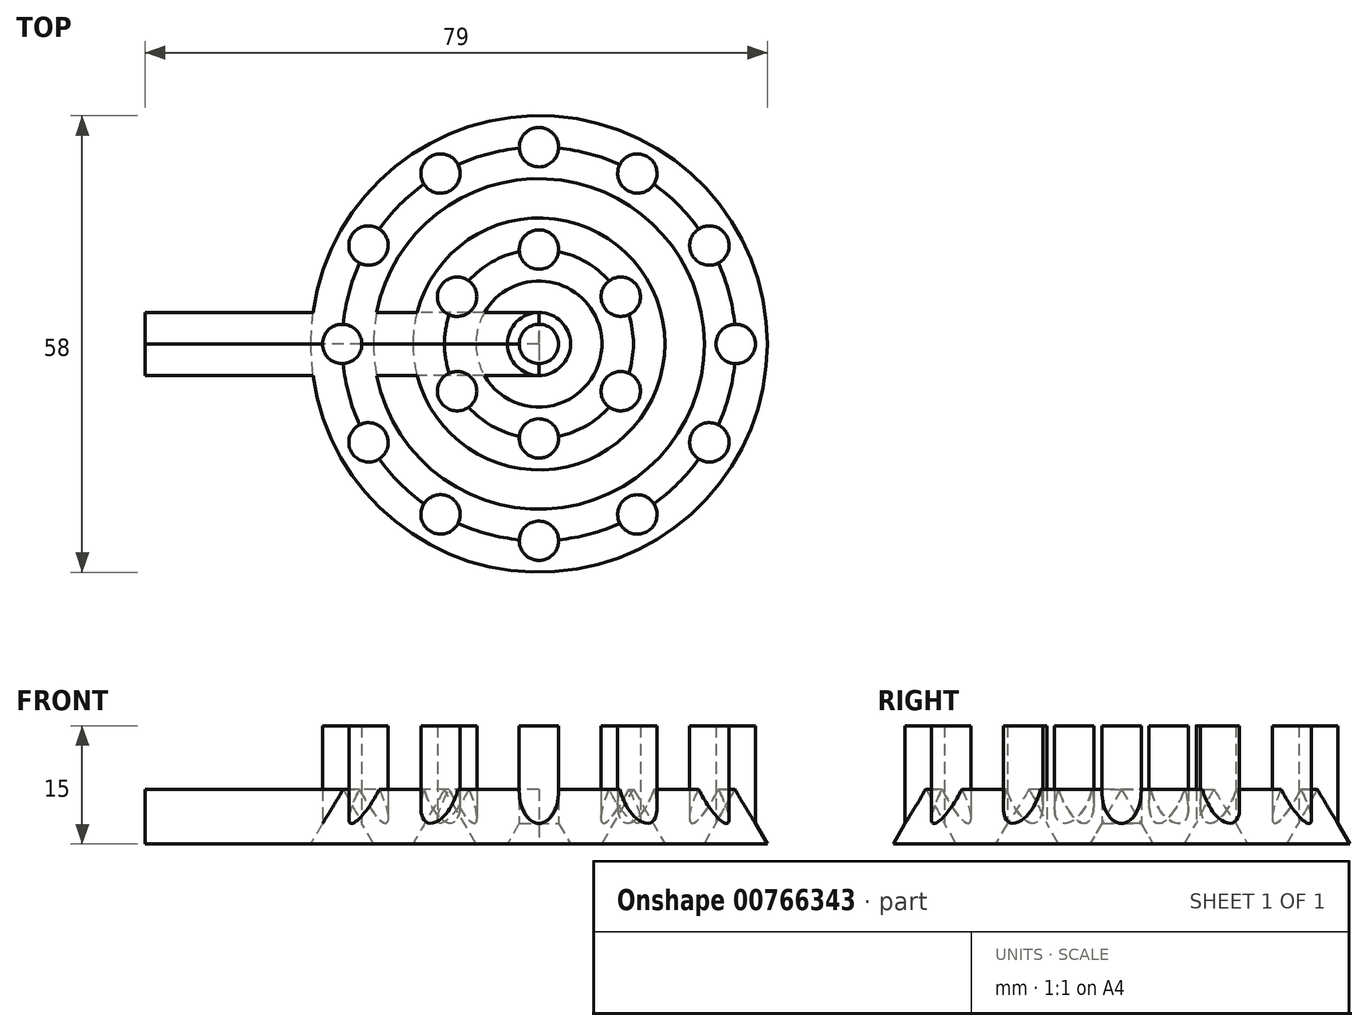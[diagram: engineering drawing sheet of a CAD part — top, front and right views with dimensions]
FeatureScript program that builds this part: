
annotation { "Feature Type Name" : "Feature", "Feature Type Description" : "" }
export const myFeature = defineFeature(function(context is Context, id is Id, definition is map)
    precondition{}
    {
        {
            var Q0;
            Q0=qCreatedBy(makeId("Top.planeOp"),FACE);
            var sketch = newSketch(context, id + "F0", { "sketchPlane" : qUnion([Q0])});
            skCircle(sketch, "E0", {"center": v(0, 0) * mm, "radius": 2.5 * mm});
            skCircle(sketch, "E1.1.0", {"center": v(12.5, 3.35) * mm, "radius": 2.5 * mm});
            skCircle(sketch, "E1.2.0", {"center": v(21.65, 12.5) * mm, "radius": 2.5 * mm});
            skPoint(sketch, "E1.center", {"position": v(0, 25) * mm});
            skCircle(sketch, "E2.1.3.0", {"center": v(25, 25) * mm, "radius": 2.5 * mm});
            skCircle(sketch, "E2.1.4.0", {"center": v(21.65, 37.5) * mm, "radius": 2.5 * mm});
            skCircle(sketch, "E2.1.5.0", {"center": v(12.5, 46.65) * mm, "radius": 2.5 * mm});
            skCircle(sketch, "E2.1.6.0", {"center": v(0, 50) * mm, "radius": 2.5 * mm});
            skCircle(sketch, "E2.1.7.0", {"center": v(-12.5, 46.65) * mm, "radius": 2.5 * mm});
            skCircle(sketch, "E2.1.8.0", {"center": v(-21.65, 37.5) * mm, "radius": 2.5 * mm});
            skCircle(sketch, "E2.1.9.0", {"center": v(-25, 25) * mm, "radius": 2.5 * mm});
            skCircle(sketch, "E2.1.10.0", {"center": v(-21.65, 12.5) * mm, "radius": 2.5 * mm});
            skCircle(sketch, "E2.1.11.0", {"center": v(-12.5, 3.35) * mm, "radius": 2.5 * mm});
            skLineSegment(sketch, "E3", {"start": v(0, 25) * mm, "end": v(0, 13) * mm, "construction": true});
            skCircle(sketch, "E4", {"center": v(0, 13) * mm, "radius": 2.5 * mm});
            skCircle(sketch, "E5", {"center": v(0, 25) * mm, "radius": 2.5 * mm});
            skCircle(sketch, "E6.1.0", {"center": v(10.4, 19) * mm, "radius": 2.5 * mm});
            skCircle(sketch, "E6.2.0", {"center": v(10.4, 31) * mm, "radius": 2.5 * mm});
            skCircle(sketch, "E6.3.0", {"center": v(0, 37) * mm, "radius": 2.5 * mm});
            skCircle(sketch, "E6.4.0", {"center": v(-10.4, 31) * mm, "radius": 2.5 * mm});
            skCircle(sketch, "E6.5.0", {"center": v(-10.4, 19) * mm, "radius": 2.5 * mm});
            skCircle(sketch, "E7", {"center": v(0, 25) * mm, "radius": 12 * mm});
            skCircle(sketch, "E8", {"center": v(0, 25) * mm, "radius": 25 * mm});
            skSolve(sketch);
        }
        {
            var Q0;
            Q0=qCreatedBy(makeId("Right.planeOp"),FACE);
            var sketch = newSketch(context, id + "F1", { "sketchPlane" : qUnion([Q0])});
            skLineSegment(sketch, "E9", {"start": v(-4, 0) * mm, "end": v(4, 0) * mm});
            skLineSegment(sketch, "E10", {"start": v(4, 0) * mm, "end": v(0, 6.93) * mm});
            skLineSegment(sketch, "E11", {"start": v(0, 6.93) * mm, "end": v(-4, 0) * mm});
            skLineSegment(sketch, "E12.1.0.0", {"start": v(25, 6.93) * mm, "end": v(21, 0) * mm});
            skLineSegment(sketch, "E12.direction1", {"start": v(-4, 0) * mm, "end": v(21, 0) * mm, "construction": true});
            skLineSegment(sketch, "E13.1.0.0", {"start": v(9, 0) * mm, "end": v(34, 0) * mm, "construction": true});
            skLineSegment(sketch, "E13.1.0.1", {"start": v(13, 6.93) * mm, "end": v(9, 0) * mm});
            skLineSegment(sketch, "E13.1.0.2", {"start": v(17, 0) * mm, "end": v(13, 6.93) * mm});
            skLineSegment(sketch, "E13.direction1", {"start": v(-4, 0) * mm, "end": v(9, 0) * mm, "construction": true});
            skLineSegment(sketch, "E14", {"start": v(25, 0) * mm, "end": v(25, 13.69) * mm});
            skLineSegment(sketch, "E15", {"start": v(21, 0) * mm, "end": v(25, 0) * mm});
            skLineSegment(sketch, "E16", {"start": v(17, 0) * mm, "end": v(9, 0) * mm});
            skLineSegment(sketch, "E17", {"start": v(25, 6.93) * mm, "end": v(29, 0) * mm});
            skLineSegment(sketch, "E18", {"start": v(29, 0) * mm, "end": v(25, 0) * mm});
            skSolve(sketch);
        }
        {
            var Q0;
            Q0=makeQuery(id+"F1.imprint","IMPRINT",FACE,{"disambiguationData":[TD([[makeQuery(id+"F1.imprint","IMPRINT",EDGE,{"derivedFrom":sQuery(id+"F1.wireOp",EDGE,"E13.1.0.1")}),1.0]])]});
            var Q1;
            Q1=makeQuery(id+"F1.imprint","IMPRINT",FACE,{"disambiguationData":[TD([[makeQuery(id+"F1.imprint","IMPRINT",EDGE,{"derivedFrom":sQuery(id+"F1.wireOp",EDGE,"E9")}),1.0]])]});
            var Q2;
            {var subQ0=sQuery(id+"F1.wireOp",EDGE,"E12.1.0.0");Q2=makeQuery(id+"F1.imprint","IMPRINT",FACE,{"disambiguationData":[TD([[makeQuery(id+"F1.imprint","IMPRINT",EDGE,{"derivedFrom":subQ0}),1.0]])]});}
            var Q3;
            Q3=sQuery(id+"F1.wireOp",EDGE,"E14");
            revolve(context, id + "F2", {"surfaceOperationType" : NewSurfaceOperationType.NEW, "entities" : qUnion([Q0, Q1, Q2]), "axis" : qUnion([Q3]), "revolveType" : RevolveType.FULL});
        }
        {
            var Q0;
            {var subQ0=sQuery(id+"F0.wireOp",EDGE,"E8");var subQ1=sQuery(id+"F0.wireOp",EDGE,"E2.1.11.0");var subQ2=makeQuery(id+"F0.imprint","INTERSECT",VERTEX,{"disambiguationData":[OD(0.0)],"derivedFrom":[subQ1,subQ0]});Q0=makeQuery(id+"F0.imprint","IMPRINT",FACE,{"disambiguationData":[TD([[makeQuery(id+"F0.imprint","IMPRINT",EDGE,{"disambiguationData":[TD([[subQ2,-1.0]])],"derivedFrom":subQ1}),1.0]])]});}
            var Q1;
            {var subQ0=sQuery(id+"F0.wireOp",EDGE,"E8");var subQ1=sQuery(id+"F0.wireOp",EDGE,"E2.1.11.0");var subQ2=makeQuery(id+"F0.imprint","INTERSECT",VERTEX,{"disambiguationData":[OD(0.0)],"derivedFrom":[subQ1,subQ0]});Q1=makeQuery(id+"F0.imprint","IMPRINT",FACE,{"disambiguationData":[TD([[makeQuery(id+"F0.imprint","IMPRINT",EDGE,{"disambiguationData":[TD([[subQ2,1.0]])],"derivedFrom":subQ1}),1.0]])]});}
            var Q2;
            {var subQ0=sQuery(id+"F0.wireOp",EDGE,"E8");var subQ1=sQuery(id+"F0.wireOp",EDGE,"E2.1.10.0");var subQ2=makeQuery(id+"F0.imprint","INTERSECT",VERTEX,{"disambiguationData":[OD(0.0)],"derivedFrom":[subQ1,subQ0]});Q2=makeQuery(id+"F0.imprint","IMPRINT",FACE,{"disambiguationData":[TD([[makeQuery(id+"F0.imprint","IMPRINT",EDGE,{"disambiguationData":[TD([[subQ2,-1.0]])],"derivedFrom":subQ1}),1.0]])]});}
            var Q3;
            {var subQ0=sQuery(id+"F0.wireOp",EDGE,"E8");var subQ1=sQuery(id+"F0.wireOp",EDGE,"E2.1.10.0");var subQ2=makeQuery(id+"F0.imprint","INTERSECT",VERTEX,{"disambiguationData":[OD(0.0)],"derivedFrom":[subQ1,subQ0]});Q3=makeQuery(id+"F0.imprint","IMPRINT",FACE,{"disambiguationData":[TD([[makeQuery(id+"F0.imprint","IMPRINT",EDGE,{"disambiguationData":[TD([[subQ2,1.0]])],"derivedFrom":subQ1}),1.0]])]});}
            var Q4;
            {var subQ0=sQuery(id+"F0.wireOp",EDGE,"E8");var subQ1=sQuery(id+"F0.wireOp",EDGE,"E2.1.9.0");var subQ2=makeQuery(id+"F0.imprint","INTERSECT",VERTEX,{"disambiguationData":[OD(0.0)],"derivedFrom":[subQ1,subQ0]});Q4=makeQuery(id+"F0.imprint","IMPRINT",FACE,{"disambiguationData":[TD([[makeQuery(id+"F0.imprint","IMPRINT",EDGE,{"disambiguationData":[TD([[subQ2,-1.0]])],"derivedFrom":subQ1}),1.0]])]});}
            var Q5;
            {var subQ0=sQuery(id+"F0.wireOp",EDGE,"E8");var subQ1=sQuery(id+"F0.wireOp",EDGE,"E2.1.9.0");var subQ2=makeQuery(id+"F0.imprint","INTERSECT",VERTEX,{"disambiguationData":[OD(0.0)],"derivedFrom":[subQ1,subQ0]});Q5=makeQuery(id+"F0.imprint","IMPRINT",FACE,{"disambiguationData":[TD([[makeQuery(id+"F0.imprint","IMPRINT",EDGE,{"disambiguationData":[TD([[subQ2,1.0]])],"derivedFrom":subQ1}),1.0]])]});}
            var Q6;
            {var subQ0=sQuery(id+"F0.wireOp",EDGE,"E8");var subQ1=sQuery(id+"F0.wireOp",EDGE,"E2.1.8.0");var subQ2=makeQuery(id+"F0.imprint","INTERSECT",VERTEX,{"disambiguationData":[OD(0.0)],"derivedFrom":[subQ1,subQ0]});Q6=makeQuery(id+"F0.imprint","IMPRINT",FACE,{"disambiguationData":[TD([[makeQuery(id+"F0.imprint","IMPRINT",EDGE,{"disambiguationData":[TD([[subQ2,1.0]])],"derivedFrom":subQ1}),1.0]])]});}
            var Q7;
            {var subQ0=sQuery(id+"F0.wireOp",EDGE,"E8");var subQ1=sQuery(id+"F0.wireOp",EDGE,"E2.1.8.0");var subQ2=makeQuery(id+"F0.imprint","INTERSECT",VERTEX,{"disambiguationData":[OD(0.0)],"derivedFrom":[subQ1,subQ0]});Q7=makeQuery(id+"F0.imprint","IMPRINT",FACE,{"disambiguationData":[TD([[makeQuery(id+"F0.imprint","IMPRINT",EDGE,{"disambiguationData":[TD([[subQ2,-1.0]])],"derivedFrom":subQ1}),1.0]])]});}
            var Q8;
            {var subQ0=sQuery(id+"F0.wireOp",EDGE,"E8");var subQ1=sQuery(id+"F0.wireOp",EDGE,"E2.1.7.0");var subQ2=makeQuery(id+"F0.imprint","INTERSECT",VERTEX,{"disambiguationData":[OD(0.0)],"derivedFrom":[subQ1,subQ0]});Q8=makeQuery(id+"F0.imprint","IMPRINT",FACE,{"disambiguationData":[TD([[makeQuery(id+"F0.imprint","IMPRINT",EDGE,{"disambiguationData":[TD([[subQ2,-1.0]])],"derivedFrom":subQ1}),1.0]])]});}
            var Q9;
            {var subQ0=sQuery(id+"F0.wireOp",EDGE,"E8");var subQ1=sQuery(id+"F0.wireOp",EDGE,"E2.1.7.0");var subQ2=makeQuery(id+"F0.imprint","INTERSECT",VERTEX,{"disambiguationData":[OD(0.0)],"derivedFrom":[subQ1,subQ0]});Q9=makeQuery(id+"F0.imprint","IMPRINT",FACE,{"disambiguationData":[TD([[makeQuery(id+"F0.imprint","IMPRINT",EDGE,{"disambiguationData":[TD([[subQ2,1.0]])],"derivedFrom":subQ1}),1.0]])]});}
            var Q10;
            {var subQ0=sQuery(id+"F0.wireOp",EDGE,"E8");var subQ1=sQuery(id+"F0.wireOp",EDGE,"E2.1.6.0");var subQ2=makeQuery(id+"F0.imprint","INTERSECT",VERTEX,{"disambiguationData":[OD(0.0)],"derivedFrom":[subQ1,subQ0]});Q10=makeQuery(id+"F0.imprint","IMPRINT",FACE,{"disambiguationData":[TD([[makeQuery(id+"F0.imprint","IMPRINT",EDGE,{"disambiguationData":[TD([[subQ2,-1.0]])],"derivedFrom":subQ1}),1.0]])]});}
            var Q11;
            {var subQ0=sQuery(id+"F0.wireOp",EDGE,"E8");var subQ1=sQuery(id+"F0.wireOp",EDGE,"E2.1.5.0");var subQ2=makeQuery(id+"F0.imprint","INTERSECT",VERTEX,{"disambiguationData":[OD(0.0)],"derivedFrom":[subQ1,subQ0]});Q11=makeQuery(id+"F0.imprint","IMPRINT",FACE,{"disambiguationData":[TD([[makeQuery(id+"F0.imprint","IMPRINT",EDGE,{"disambiguationData":[TD([[subQ2,-1.0]])],"derivedFrom":subQ1}),1.0]])]});}
            var Q12;
            {var subQ0=sQuery(id+"F0.wireOp",EDGE,"E8");var subQ1=sQuery(id+"F0.wireOp",EDGE,"E2.1.4.0");var subQ2=makeQuery(id+"F0.imprint","INTERSECT",VERTEX,{"disambiguationData":[OD(0.0)],"derivedFrom":[subQ1,subQ0]});Q12=makeQuery(id+"F0.imprint","IMPRINT",FACE,{"disambiguationData":[TD([[makeQuery(id+"F0.imprint","IMPRINT",EDGE,{"disambiguationData":[TD([[subQ2,1.0]])],"derivedFrom":subQ1}),1.0]])]});}
            var Q13;
            {var subQ0=sQuery(id+"F0.wireOp",EDGE,"E8");var subQ1=sQuery(id+"F0.wireOp",EDGE,"E0");var subQ2=makeQuery(id+"F0.imprint","INTERSECT",VERTEX,{"disambiguationData":[OD(0.0)],"derivedFrom":[subQ1,subQ0]});Q13=makeQuery(id+"F0.imprint","IMPRINT",FACE,{"disambiguationData":[TD([[makeQuery(id+"F0.imprint","IMPRINT",EDGE,{"disambiguationData":[TD([[subQ2,1.0]])],"derivedFrom":subQ1}),1.0]])]});}
            var Q14;
            {var subQ0=sQuery(id+"F0.wireOp",EDGE,"E8");var subQ1=sQuery(id+"F0.wireOp",EDGE,"E1.1.0");var subQ2=makeQuery(id+"F0.imprint","INTERSECT",VERTEX,{"disambiguationData":[OD(0.0)],"derivedFrom":[subQ1,subQ0]});Q14=makeQuery(id+"F0.imprint","IMPRINT",FACE,{"disambiguationData":[TD([[makeQuery(id+"F0.imprint","IMPRINT",EDGE,{"disambiguationData":[TD([[subQ2,-1.0]])],"derivedFrom":subQ1}),1.0]])]});}
            var Q15;
            {var subQ0=sQuery(id+"F0.wireOp",EDGE,"E8");var subQ1=sQuery(id+"F0.wireOp",EDGE,"E1.1.0");var subQ2=makeQuery(id+"F0.imprint","INTERSECT",VERTEX,{"disambiguationData":[OD(0.0)],"derivedFrom":[subQ1,subQ0]});Q15=makeQuery(id+"F0.imprint","IMPRINT",FACE,{"disambiguationData":[TD([[makeQuery(id+"F0.imprint","IMPRINT",EDGE,{"disambiguationData":[TD([[subQ2,1.0]])],"derivedFrom":subQ1}),1.0]])]});}
            var Q16;
            {var subQ0=sQuery(id+"F0.wireOp",EDGE,"E8");var subQ1=sQuery(id+"F0.wireOp",EDGE,"E1.2.0");var subQ2=makeQuery(id+"F0.imprint","INTERSECT",VERTEX,{"disambiguationData":[OD(0.0)],"derivedFrom":[subQ1,subQ0]});Q16=makeQuery(id+"F0.imprint","IMPRINT",FACE,{"disambiguationData":[TD([[makeQuery(id+"F0.imprint","IMPRINT",EDGE,{"disambiguationData":[TD([[subQ2,-1.0]])],"derivedFrom":subQ1}),1.0]])]});}
            var Q17;
            {var subQ0=sQuery(id+"F0.wireOp",EDGE,"E8");var subQ1=sQuery(id+"F0.wireOp",EDGE,"E1.2.0");var subQ2=makeQuery(id+"F0.imprint","INTERSECT",VERTEX,{"disambiguationData":[OD(0.0)],"derivedFrom":[subQ1,subQ0]});Q17=makeQuery(id+"F0.imprint","IMPRINT",FACE,{"disambiguationData":[TD([[makeQuery(id+"F0.imprint","IMPRINT",EDGE,{"disambiguationData":[TD([[subQ2,1.0]])],"derivedFrom":subQ1}),1.0]])]});}
            var Q18;
            {var subQ0=sQuery(id+"F0.wireOp",EDGE,"E8");var subQ1=sQuery(id+"F0.wireOp",EDGE,"E2.1.3.0");var subQ2=makeQuery(id+"F0.imprint","INTERSECT",VERTEX,{"disambiguationData":[OD(0.0)],"derivedFrom":[subQ1,subQ0]});Q18=makeQuery(id+"F0.imprint","IMPRINT",FACE,{"disambiguationData":[TD([[makeQuery(id+"F0.imprint","IMPRINT",EDGE,{"disambiguationData":[TD([[subQ2,1.0]])],"derivedFrom":subQ1}),1.0]])]});}
            var Q19;
            {var subQ0=sQuery(id+"F0.wireOp",EDGE,"E8");var subQ1=sQuery(id+"F0.wireOp",EDGE,"E2.1.3.0");var subQ2=makeQuery(id+"F0.imprint","INTERSECT",VERTEX,{"disambiguationData":[OD(0.0)],"derivedFrom":[subQ1,subQ0]});Q19=makeQuery(id+"F0.imprint","IMPRINT",FACE,{"disambiguationData":[TD([[makeQuery(id+"F0.imprint","IMPRINT",EDGE,{"disambiguationData":[TD([[subQ2,-1.0]])],"derivedFrom":subQ1}),1.0]])]});}
            var Q20;
            {var subQ0=sQuery(id+"F0.wireOp",EDGE,"E7");var subQ1=sQuery(id+"F0.wireOp",EDGE,"E6.1.0");var subQ2=makeQuery(id+"F0.imprint","INTERSECT",VERTEX,{"disambiguationData":[OD(0.0)],"derivedFrom":[subQ1,subQ0]});Q20=makeQuery(id+"F0.imprint","IMPRINT",FACE,{"disambiguationData":[TD([[makeQuery(id+"F0.imprint","IMPRINT",EDGE,{"disambiguationData":[TD([[subQ2,-1.0]])],"derivedFrom":subQ1}),1.0]])]});}
            var Q21;
            {var subQ0=sQuery(id+"F0.wireOp",EDGE,"E7");var subQ1=sQuery(id+"F0.wireOp",EDGE,"E6.1.0");var subQ2=makeQuery(id+"F0.imprint","INTERSECT",VERTEX,{"disambiguationData":[OD(0.0)],"derivedFrom":[subQ1,subQ0]});Q21=makeQuery(id+"F0.imprint","IMPRINT",FACE,{"disambiguationData":[TD([[makeQuery(id+"F0.imprint","IMPRINT",EDGE,{"disambiguationData":[TD([[subQ2,1.0]])],"derivedFrom":subQ1}),1.0]])]});}
            var Q22;
            {var subQ0=sQuery(id+"F0.wireOp",EDGE,"E7");var subQ1=sQuery(id+"F0.wireOp",EDGE,"E6.2.0");var subQ2=makeQuery(id+"F0.imprint","INTERSECT",VERTEX,{"disambiguationData":[OD(0.0)],"derivedFrom":[subQ1,subQ0]});Q22=makeQuery(id+"F0.imprint","IMPRINT",FACE,{"disambiguationData":[TD([[makeQuery(id+"F0.imprint","IMPRINT",EDGE,{"disambiguationData":[TD([[subQ2,1.0]])],"derivedFrom":subQ1}),1.0]])]});}
            var Q23;
            {var subQ0=sQuery(id+"F0.wireOp",EDGE,"E7");var subQ1=sQuery(id+"F0.wireOp",EDGE,"E6.3.0");var subQ2=makeQuery(id+"F0.imprint","INTERSECT",VERTEX,{"disambiguationData":[OD(0.0)],"derivedFrom":[subQ1,subQ0]});Q23=makeQuery(id+"F0.imprint","IMPRINT",FACE,{"disambiguationData":[TD([[makeQuery(id+"F0.imprint","IMPRINT",EDGE,{"disambiguationData":[TD([[subQ2,1.0]])],"derivedFrom":subQ1}),1.0]])]});}
            var Q24;
            {var subQ0=sQuery(id+"F0.wireOp",EDGE,"E7");var subQ1=sQuery(id+"F0.wireOp",EDGE,"E6.3.0");var subQ2=makeQuery(id+"F0.imprint","INTERSECT",VERTEX,{"disambiguationData":[OD(0.0)],"derivedFrom":[subQ1,subQ0]});Q24=makeQuery(id+"F0.imprint","IMPRINT",FACE,{"disambiguationData":[TD([[makeQuery(id+"F0.imprint","IMPRINT",EDGE,{"disambiguationData":[TD([[subQ2,-1.0]])],"derivedFrom":subQ1}),1.0]])]});}
            var Q25;
            Q25=makeQuery(id+"F0.imprint","IMPRINT",FACE,{"disambiguationData":[TD([[makeQuery(id+"F0.imprint","IMPRINT",EDGE,{"derivedFrom":sQuery(id+"F0.wireOp",EDGE,"E5")}),1.0]])]});
            var Q26;
            {var subQ0=sQuery(id+"F0.wireOp",EDGE,"E7");var subQ1=sQuery(id+"F0.wireOp",EDGE,"E6.2.0");var subQ2=makeQuery(id+"F0.imprint","INTERSECT",VERTEX,{"disambiguationData":[OD(0.0)],"derivedFrom":[subQ1,subQ0]});Q26=makeQuery(id+"F0.imprint","IMPRINT",FACE,{"disambiguationData":[TD([[makeQuery(id+"F0.imprint","IMPRINT",EDGE,{"disambiguationData":[TD([[subQ2,-1.0]])],"derivedFrom":subQ1}),1.0]])]});}
            var Q27;
            {var subQ0=sQuery(id+"F0.wireOp",EDGE,"E7");var subQ1=sQuery(id+"F0.wireOp",EDGE,"E4");var subQ2=makeQuery(id+"F0.imprint","INTERSECT",VERTEX,{"disambiguationData":[OD(0.0)],"derivedFrom":[subQ1,subQ0]});Q27=makeQuery(id+"F0.imprint","IMPRINT",FACE,{"disambiguationData":[TD([[makeQuery(id+"F0.imprint","IMPRINT",EDGE,{"disambiguationData":[TD([[subQ2,-1.0]])],"derivedFrom":subQ1}),1.0]])]});}
            var Q28;
            {var subQ0=sQuery(id+"F0.wireOp",EDGE,"E7");var subQ1=sQuery(id+"F0.wireOp",EDGE,"E6.5.0");var subQ2=makeQuery(id+"F0.imprint","INTERSECT",VERTEX,{"disambiguationData":[OD(0.0)],"derivedFrom":[subQ1,subQ0]});Q28=makeQuery(id+"F0.imprint","IMPRINT",FACE,{"disambiguationData":[TD([[makeQuery(id+"F0.imprint","IMPRINT",EDGE,{"disambiguationData":[TD([[subQ2,-1.0]])],"derivedFrom":subQ1}),1.0]])]});}
            var Q29;
            {var subQ0=sQuery(id+"F0.wireOp",EDGE,"E7");var subQ1=sQuery(id+"F0.wireOp",EDGE,"E6.5.0");var subQ2=makeQuery(id+"F0.imprint","INTERSECT",VERTEX,{"disambiguationData":[OD(0.0)],"derivedFrom":[subQ1,subQ0]});Q29=makeQuery(id+"F0.imprint","IMPRINT",FACE,{"disambiguationData":[TD([[makeQuery(id+"F0.imprint","IMPRINT",EDGE,{"disambiguationData":[TD([[subQ2,1.0]])],"derivedFrom":subQ1}),1.0]])]});}
            var Q30;
            {var subQ0=sQuery(id+"F0.wireOp",EDGE,"E7");var subQ1=sQuery(id+"F0.wireOp",EDGE,"E4");var subQ2=makeQuery(id+"F0.imprint","INTERSECT",VERTEX,{"disambiguationData":[OD(0.0)],"derivedFrom":[subQ1,subQ0]});Q30=makeQuery(id+"F0.imprint","IMPRINT",FACE,{"disambiguationData":[TD([[makeQuery(id+"F0.imprint","IMPRINT",EDGE,{"disambiguationData":[TD([[subQ2,1.0]])],"derivedFrom":subQ1}),1.0]])]});}
            var Q31;
            {var subQ0=sQuery(id+"F0.wireOp",EDGE,"E7");var subQ1=sQuery(id+"F0.wireOp",EDGE,"E6.4.0");var subQ2=makeQuery(id+"F0.imprint","INTERSECT",VERTEX,{"disambiguationData":[OD(0.0)],"derivedFrom":[subQ1,subQ0]});Q31=makeQuery(id+"F0.imprint","IMPRINT",FACE,{"disambiguationData":[TD([[makeQuery(id+"F0.imprint","IMPRINT",EDGE,{"disambiguationData":[TD([[subQ2,1.0]])],"derivedFrom":subQ1}),1.0]])]});}
            var Q32;
            {var subQ0=sQuery(id+"F0.wireOp",EDGE,"E7");var subQ1=sQuery(id+"F0.wireOp",EDGE,"E6.4.0");var subQ2=makeQuery(id+"F0.imprint","INTERSECT",VERTEX,{"disambiguationData":[OD(0.0)],"derivedFrom":[subQ1,subQ0]});Q32=makeQuery(id+"F0.imprint","IMPRINT",FACE,{"disambiguationData":[TD([[makeQuery(id+"F0.imprint","IMPRINT",EDGE,{"disambiguationData":[TD([[subQ2,-1.0]])],"derivedFrom":subQ1}),1.0]])]});}
            var Q33;
            {var subQ0=sQuery(id+"F0.wireOp",EDGE,"E8");var subQ1=sQuery(id+"F0.wireOp",EDGE,"E0");var subQ2=makeQuery(id+"F0.imprint","INTERSECT",VERTEX,{"disambiguationData":[OD(0.0)],"derivedFrom":[subQ1,subQ0]});Q33=makeQuery(id+"F0.imprint","IMPRINT",FACE,{"disambiguationData":[TD([[makeQuery(id+"F0.imprint","IMPRINT",EDGE,{"disambiguationData":[TD([[subQ2,-1.0]])],"derivedFrom":subQ1}),1.0]])]});}
            var Q34;
            {var subQ0=sQuery(id+"F0.wireOp",EDGE,"E8");var subQ1=sQuery(id+"F0.wireOp",EDGE,"E2.1.6.0");var subQ2=makeQuery(id+"F0.imprint","INTERSECT",VERTEX,{"disambiguationData":[OD(0.0)],"derivedFrom":[subQ1,subQ0]});Q34=makeQuery(id+"F0.imprint","IMPRINT",FACE,{"disambiguationData":[TD([[makeQuery(id+"F0.imprint","IMPRINT",EDGE,{"disambiguationData":[TD([[subQ2,1.0]])],"derivedFrom":subQ1}),1.0]])]});}
            var Q35;
            {var subQ0=sQuery(id+"F0.wireOp",EDGE,"E8");var subQ1=sQuery(id+"F0.wireOp",EDGE,"E2.1.4.0");var subQ2=makeQuery(id+"F0.imprint","INTERSECT",VERTEX,{"disambiguationData":[OD(0.0)],"derivedFrom":[subQ1,subQ0]});Q35=makeQuery(id+"F0.imprint","IMPRINT",FACE,{"disambiguationData":[TD([[makeQuery(id+"F0.imprint","IMPRINT",EDGE,{"disambiguationData":[TD([[subQ2,-1.0]])],"derivedFrom":subQ1}),1.0]])]});}
            var Q36;
            {var subQ0=sQuery(id+"F0.wireOp",EDGE,"E8");var subQ1=sQuery(id+"F0.wireOp",EDGE,"E2.1.5.0");var subQ2=makeQuery(id+"F0.imprint","INTERSECT",VERTEX,{"disambiguationData":[OD(0.0)],"derivedFrom":[subQ1,subQ0]});Q36=makeQuery(id+"F0.imprint","IMPRINT",FACE,{"disambiguationData":[TD([[makeQuery(id+"F0.imprint","IMPRINT",EDGE,{"disambiguationData":[TD([[subQ2,1.0]])],"derivedFrom":subQ1}),1.0]])]});}
            extrude(context, id + "F3", {"entities" : qUnion([Q0, Q1, Q2, Q3, Q4, Q5, Q6, Q7, Q8, Q9, Q10, Q11, Q12, Q13, Q14, Q15, Q16, Q17, Q18, Q19, Q20, Q21, Q22, Q23, Q24, Q25, Q26, Q27, Q28, Q29, Q30, Q31, Q32, Q33, Q34, Q35, Q36]), "operationType" : NewBodyOperationType.ADD, "depth" : 15 * mm, "offsetDistance" : 25 * mm});
        }
        {
            var Q0;
            Q0=qCreatedBy(makeId("Front.planeOp"),FACE);
            var sketch = newSketch(context, id + "F4", { "sketchPlane" : qUnion([Q0])});
            skLineSegment(sketch, "E19", {"start": v(0, 0) * mm, "end": v(-50, 0) * mm});
            skSolve(sketch);
        }
        {
            var Q0;
            {var subQ0=sQuery(id+"F1.wireOp",EDGE,"E17");Q0=makeQuery(id+"F1.imprint","IMPRINT",FACE,{"disambiguationData":[TD([[makeQuery(id+"F1.imprint","IMPRINT",EDGE,{"derivedFrom":subQ0}),-1.0]])]});}
            var Q1;
            {var subQ0=sQuery(id+"F1.wireOp",EDGE,"E12.1.0.0");Q1=makeQuery(id+"F1.imprint","IMPRINT",FACE,{"disambiguationData":[TD([[makeQuery(id+"F1.imprint","IMPRINT",EDGE,{"derivedFrom":subQ0}),1.0]])]});}
            var Q2;
            Q2=sQuery(id+"F4.wireOp",EDGE,"E19");
            sweep(context, id + "F5", {"profiles" : qUnion([Q0, Q1]), "path" : qUnion([Q2])});
        }
    });
